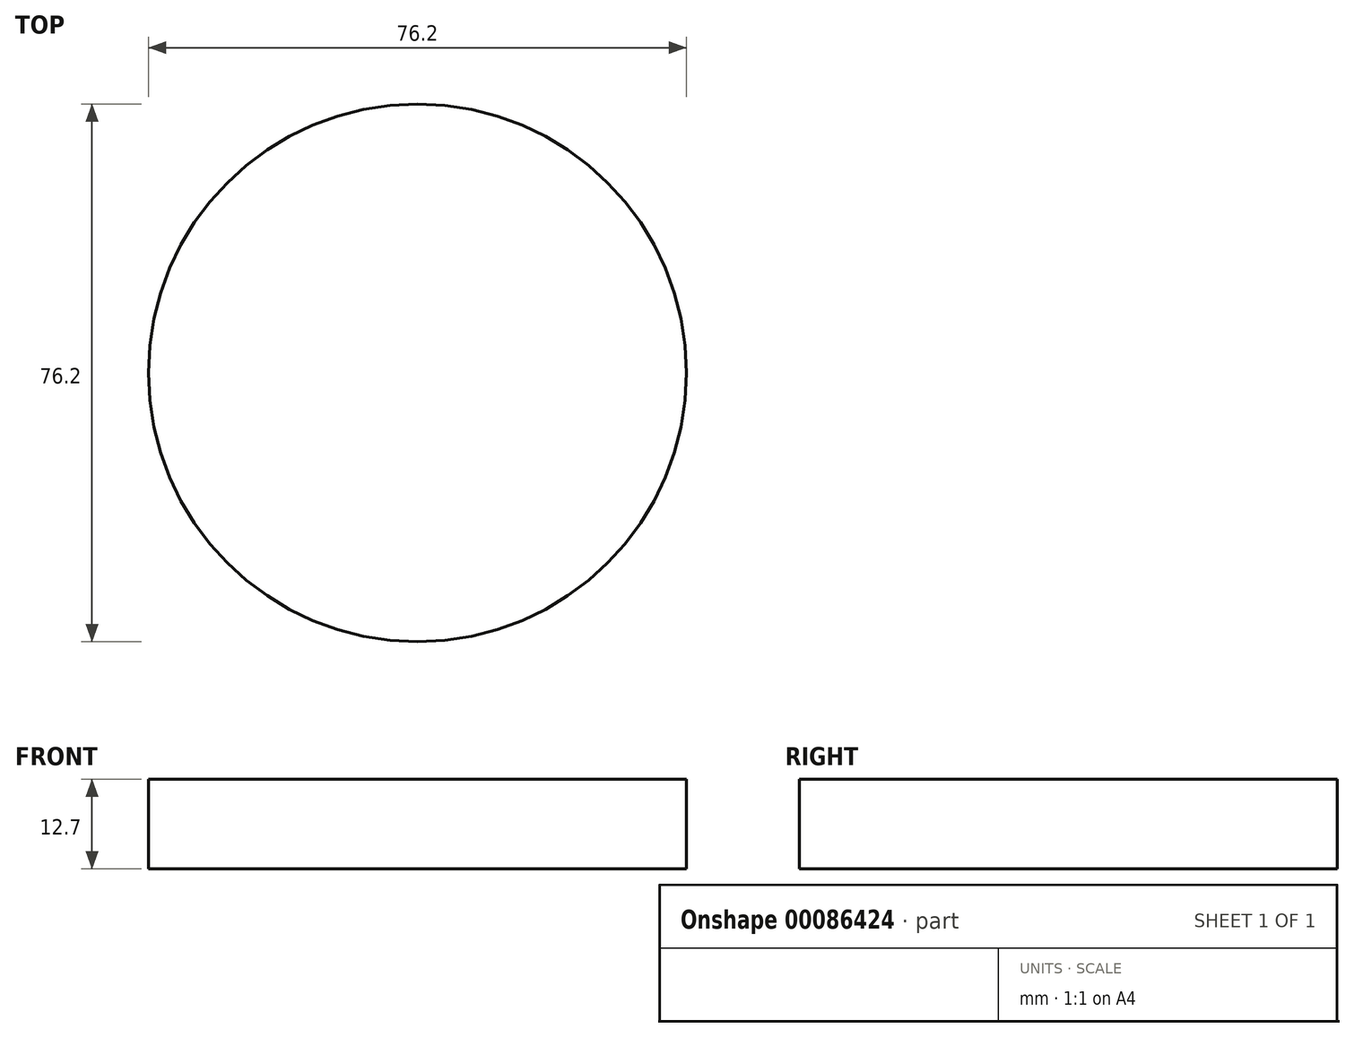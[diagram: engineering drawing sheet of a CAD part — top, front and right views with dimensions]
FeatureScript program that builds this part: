
annotation { "Feature Type Name" : "Feature", "Feature Type Description" : "" }
export const myFeature = defineFeature(function(context is Context, id is Id, definition is map)
    precondition{}
    {
        {
            var Q0;
            Q0=qCreatedBy(makeId("Top.planeOp"),FACE);
            var sketch = newSketch(context, id + "F0", { "sketchPlane" : qUnion([Q0])});
            skCircle(sketch, "E0", {"center": v(0, 0) * mm, "radius": 38.1 * mm});
            skSolve(sketch);
        }
        {
            var Q0;
            Q0=makeQuery(id+"F0.imprint","IMPRINT",FACE,{"disambiguationData":[TD([[makeQuery(id+"F0.imprint","IMPRINT",EDGE,{"derivedFrom":sQuery(id+"F0.wireOp",EDGE,"E0")}),1.0]])]});
            extrude(context, id + "F1", {"entities" : qUnion([Q0]), "endBound" : BoundingType.SYMMETRIC, "depth" : 12.7 * mm});
        }
    });
